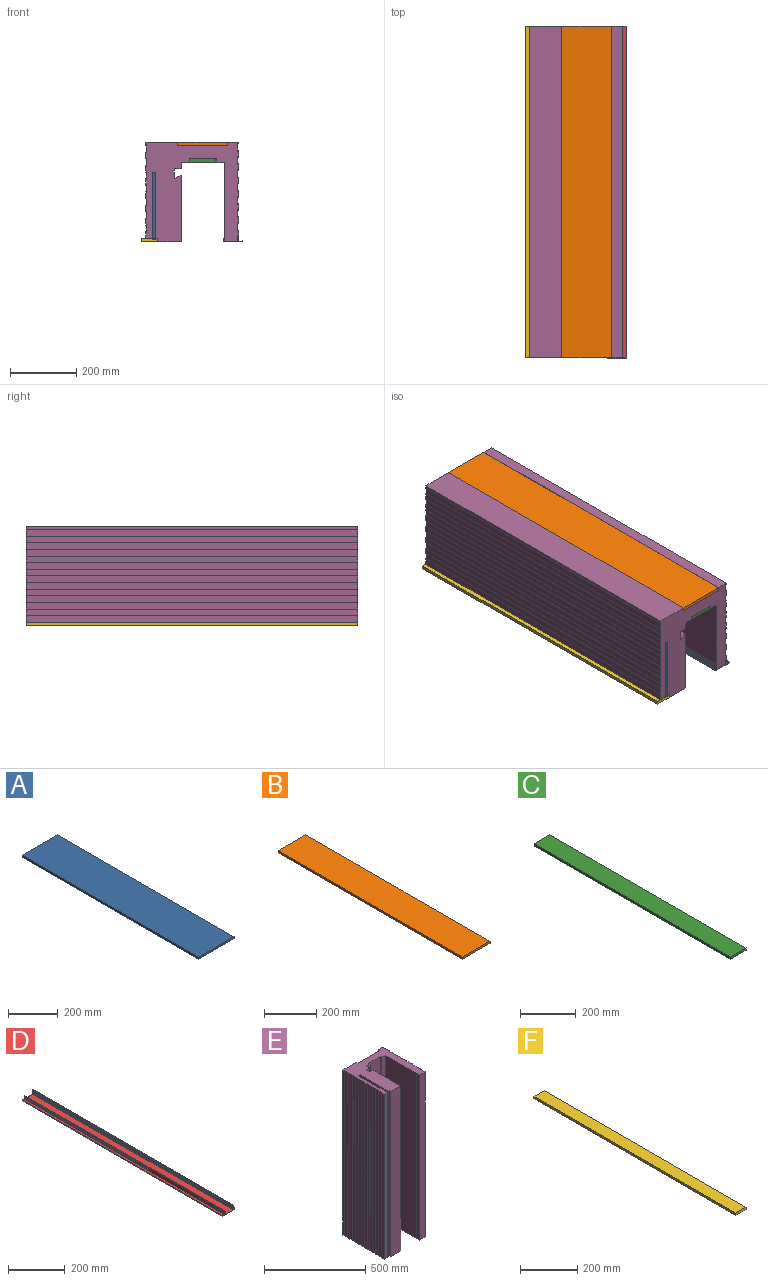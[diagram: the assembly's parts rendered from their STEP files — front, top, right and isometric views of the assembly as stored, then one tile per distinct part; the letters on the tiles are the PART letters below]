
ASSEMBLY  parts=6 mates=5
PART A: 6 faces, bbox 200x1000x10 mm
  f0: plane 1000x10mm, normal (-1,0,0), area 10000mm2, adj f1,f3,f4,f5
  f1: plane 1000x200mm, normal (0,0,-1), area 200000mm2, adj f0,f2,f4,f5
  f2: plane 1000x10mm, normal (1,0,0), area 10000mm2, adj f1,f3,f4,f5
  f3: plane 1000x200mm, normal (0,0,1), area 200000mm2, adj f0,f2,f4,f5
  f4: plane 200x10mm, normal (0,-1,0), area 2000mm2, adj f0,f1,f2,f3
  f5: plane 200x10mm, normal (0,1,0), area 2000mm2, adj f0,f1,f2,f3
PART B: 6 faces, bbox 150x1000x10 mm
  f0: plane 1000x10mm, normal (-1,0,0), area 10000mm2, adj f1,f3,f4,f5
  f1: plane 1000x150mm, normal (0,0,-1), area 150000mm2, adj f0,f2,f4,f5
  f2: plane 1000x10mm, normal (1,0,0), area 10000mm2, adj f1,f3,f4,f5
  f3: plane 1000x150mm, normal (0,0,1), area 150000mm2, adj f0,f2,f4,f5
  f4: plane 150x10mm, normal (0,-1,0), area 1500mm2, adj f0,f1,f2,f3
  f5: plane 150x10mm, normal (0,1,0), area 1500mm2, adj f0,f1,f2,f3
PART C: 6 faces, bbox 80x1000x10 mm
  f0: plane 1000x10mm, normal (-1,0,0), area 10000mm2, adj f1,f3,f4,f5
  f1: plane 1000x80mm, normal (0,0,-1), area 80000mm2, adj f0,f2,f4,f5
  f2: plane 1000x10mm, normal (1,0,0), area 10000mm2, adj f1,f3,f4,f5
  f3: plane 1000x80mm, normal (0,0,1), area 80000mm2, adj f0,f2,f4,f5
  f4: plane 80x10mm, normal (0,-1,0), area 800mm2, adj f0,f1,f2,f3
  f5: plane 80x10mm, normal (0,1,0), area 800mm2, adj f0,f1,f2,f3
PART D: 62 faces, bbox 57.5x1000x21 mm
  f0: plane 1000x14.3mm, normal (-1,0,0), area 14303.9mm2, adj f1,f2,f60,f61
  f1: plane 57.5x21mm, normal (0,-1,0), area 145.8mm2, adj f0,f2,f3,f4,f5,f6,f7,f8
  f2: plane 1000x11mm, normal (0,0,1), area 11000mm2, adj f0,f1,f3,f60
  f3: plane 1000x1.5mm, normal (1,0,0), area 1500mm2, adj f1,f2,f4,f60
  f4: plane 1000x1.5mm, normal (0,0,1), area 1500mm2, adj f1,f3,f5,f60
  f5: plane 1000x3mm, normal (-1,0,0), area 3000mm2, adj f1,f4,f6,f60
  f6: plane 1000x57.5mm, normal (0,0,-1), area 57500mm2, adj f1,f5,f7,f60
  f7: plane 1000x4mm, normal (1,0,0), area 4000mm2, adj f1,f6,f8,f60
  f8: plane 1000x1mm, normal (0,0,1), area 1000mm2, adj f1,f7,f9,f60
  f9: plane 1000x3mm, normal (-1,0,0), area 3000mm2, adj f1,f8,f10,f60
  f10: plane 1000x1mm, normal (0,0,1), area 1000mm2, adj f1,f9,f11,f60
  f11: plane 1000x7mm, normal (1,0,0), area 7000mm2, adj f1,f10,f12,f60
  f12: plane 1000x1mm, normal (0,0,-1), area 1000mm2, adj f1,f11,f13,f60
  f13: plane 1000x3mm, normal (-1,0,0), area 3000mm2, adj f1,f12,f14,f60
  f14: plane 1000x1mm, normal (0,0,-1), area 1000mm2, adj f1,f13,f15,f60
  f15: plane 1000x4mm, normal (1,0,0), area 4000mm2, adj f1,f14,f16,f60
  f16: plane 1000x2mm, normal (0,0,1), area 2000mm2, adj f1,f15,f17,f60
  f17: plane 1000x12mm, normal (1,0,0), area 12000mm2, adj f1,f16,f18,f60
  f18: plane 1000x1mm, normal (0,0,1), area 1000mm2, adj f1,f17,f19,f60
  f19: plane 1000x1.73mm, normal (-0.87,0,0.5), area 2000mm2, adj f1,f18,f20,f60
  f20: plane 1000x1mm, normal (0,0,-1), area 1000mm2, adj f1,f19,f21,f60
  f21: plane 1000x1.73mm, normal (-0.87,0,0.5), area 2000mm2, adj f1,f20,f22,f60
  f22: plane 1000x1mm, normal (0,0,-1), area 1000mm2, adj f1,f21,f23,f60
  f23: plane 1000x1.73mm, normal (-0.87,0,0.5), area 2000mm2, adj f1,f22,f24,f60
  f24: plane 1000x1mm, normal (0,0,-1), area 1000mm2, adj f1,f23,f25,f60
  f25: plane 1000x1.73mm, normal (-0.87,0,0.5), area 2000mm2, adj f1,f24,f26,f60
  f26: plane 1000x1mm, normal (0,0,-1), area 1000mm2, adj f1,f25,f27,f60
  f27: plane 1000x1.73mm, normal (-0.87,0,0.5), area 2000mm2, adj f1,f26,f28,f60
  f28: plane 1000x1mm, normal (0,0,-1), area 1000mm2, adj f1,f27,f29,f60
  f29: plane 1000x1.73mm, normal (-0.87,0,0.5), area 2000mm2, adj f1,f28,f30,f60
  f30: plane 1000x1mm, normal (0,0,-1), area 1000mm2, adj f1,f29,f31,f60
  f31: plane 1000x1.73mm, normal (-0.87,0,0.5), area 2000mm2, adj f1,f30,f32,f60
  f32: plane 1000x1mm, normal (0,0,-1), area 1000mm2, adj f1,f31,f33,f60
  f33: plane 1000x1.73mm, normal (-0.87,0,0.5), area 2000mm2, adj f1,f32,f34,f60
  f34: plane 1000x1mm, normal (0,0,-1), area 1000mm2, adj f1,f33,f35,f60
  f35: plane 1000x1.73mm, normal (-0.87,0,0.5), area 2000mm2, adj f1,f34,f36,f60
  f36: plane 1000x1mm, normal (0,0,-1), area 1000mm2, adj f1,f35,f37,f60
  f37: plane 1000x1.73mm, normal (-0.87,0,0.5), area 2000mm2, adj f1,f36,f38,f60
  f38: plane 1000x1mm, normal (0,0,-1), area 1000mm2, adj f1,f37,f39,f60
  f39: plane 1000x1.73mm, normal (-0.87,0,0.5), area 2000mm2, adj f1,f38,f40,f60
  f40: plane 1000x1mm, normal (0,0,-1), area 1000mm2, adj f1,f39,f41,f60
  f41: plane 1000x0.45mm, normal (-1,0,0), area 447.4mm2, adj f1,f40,f42,f60
  f42: plane 1000x41mm, normal (0,0,1), area 41000mm2, adj f1,f41,f43,f60
  f43: plane 1000x0.45mm, normal (1,0,0), area 447.4mm2, adj f1,f42,f44,f60
  f44: plane 1000x1mm, normal (0,0,-1), area 1000mm2, adj f1,f43,f45,f60
  f45: plane 1000x1.73mm, normal (0.87,0,0.5), area 2000mm2, adj f1,f44,f46,f60
  f46: plane 1000x1mm, normal (0,0,-1), area 1000mm2, adj f1,f45,f47,f60
  f47: plane 1000x1.73mm, normal (0.87,0,0.5), area 2000mm2, adj f1,f46,f48,f60
  f48: plane 1000x1mm, normal (0,0,-1), area 1000mm2, adj f1,f47,f49,f60
  f49: plane 1000x1.73mm, normal (0.87,0,0.5), area 2000mm2, adj f1,f48,f50,f60
  f50: plane 1000x1mm, normal (0,0,-1), area 1000mm2, adj f1,f49,f51,f60
  f51: plane 1000x1.73mm, normal (0.87,0,0.5), area 2000mm2, adj f1,f50,f52,f60
  f52: plane 1000x1mm, normal (0,0,-1), area 1000mm2, adj f1,f51,f53,f60
  f53: plane 1000x1.73mm, normal (0.87,0,0.5), area 2000mm2, adj f1,f52,f54,f60
  f54: plane 1000x1mm, normal (0,0,-1), area 1000mm2, adj f1,f53,f55,f60
  f55: plane 1000x1.73mm, normal (0.87,0,0.5), area 2000mm2, adj f1,f54,f56,f60
  f56: plane 1000x1mm, normal (0,0,-1), area 1000mm2, adj f1,f55,f57,f60
  f57: plane 1000x1.73mm, normal (0.87,0,0.5), area 2000mm2, adj f1,f56,f58,f60
  f58: plane 1000x1mm, normal (0,0,-1), area 1000mm2, adj f1,f57,f59,f60
  f59: plane 1000x1.73mm, normal (0.87,0,0.5), area 2000mm2, adj f1,f58,f60,f61
  f60: plane 57.5x21mm, normal (0,1,0), area 145.8mm2, adj f0,f2,f3,f4,f5,f6,f7,f8
  f61: plane 1000x1mm, normal (0,0,1), area 1000mm2, adj f0,f1,f59,f60
PART E: 88 faces, bbox 280x300x1000 mm
  f0: plane 1000x20mm, normal (-1,0,0), area 20000mm2, adj f44,f45,f82,f86
  f1: plane 1000x20mm, normal (-1,0,0), area 20000mm2, adj f44,f45,f79,f83
  f2: plane 1000x20mm, normal (-1,0,0), area 20000mm2, adj f44,f45,f76,f80
  f3: plane 1000x20mm, normal (-1,0,0), area 20000mm2, adj f44,f45,f73,f77
  f4: plane 1000x20mm, normal (-1,0,0), area 20000mm2, adj f44,f45,f70,f74
  f5: plane 1000x20mm, normal (-1,0,0), area 20000mm2, adj f44,f45,f67,f71
  f6: plane 1000x10mm, normal (-1,0,0), area 10000mm2, adj f15,f44,f45,f68
  f7: plane 1000x15mm, normal (1,0,0), area 15000mm2, adj f39,f44,f45,f64
  f8: plane 1000x20mm, normal (1,0,0), area 20000mm2, adj f44,f45,f61,f65
  f9: plane 1000x20mm, normal (1,0,0), area 20000mm2, adj f44,f45,f58,f62
  f10: plane 1000x20mm, normal (1,0,0), area 20000mm2, adj f44,f45,f55,f59
  f11: plane 1000x20mm, normal (1,0,0), area 20000mm2, adj f44,f45,f52,f56
  f12: plane 1000x20mm, normal (1,0,0), area 20000mm2, adj f44,f45,f49,f53
  f13: plane 1000x20mm, normal (1,0,0), area 20000mm2, adj f44,f45,f46,f50
  f14: plane 1000x10mm, normal (1,0,0), area 10000mm2, adj f15,f43,f44,f45
  f15: plane 1000x96.75mm, normal (0,1,0), area 96750mm2, adj f6,f14,f44,f45
  f16: plane 1000x20mm, normal (-1,0,0), area 20000mm2, adj f17,f44,f45,f85
  f17: plane 1000x20.5mm, normal (0,-1,0), area 20500mm2, adj f16,f18,f44,f45
  f18: plane 1000x200mm, normal (1,0,0), area 200000mm2, adj f17,f19,f44,f45
  f19: cylinder r=10mm len=1000mm, axis (0,0,-1), area 11054.3mm2, adj f18,f20,f44,f45
  f20: plane 1000x200mm, normal (-1,0,0), area 200000mm2, adj f19,f21,f44,f45
  f21: plane 1000x6mm, normal (0,-1,0), area 6000mm2, adj f20,f22,f44,f45
  f22: plane 1000x10mm, normal (-1,0,0), area 10000mm2, adj f21,f23,f44,f45
  f23: plane 1000x70mm, normal (0,-1,0), area 70000mm2, adj f22,f24,f44,f45
  f24: plane 1000x200.19mm, normal (1,0,0), area 200190.5mm2, adj f23,f25,f44,f45
  f25: plane 1000x20mm, normal (-0.45,0.89,0), area 22446.5mm2, adj f24,f26,f44,f45
  f26: plane 1000x30mm, normal (1,0,0), area 30000mm2, adj f25,f27,f44,f45
  f27: plane 1000x20mm, normal (0,-1,0), area 20000mm2, adj f26,f28,f44,f45
  f28: plane 1000x20mm, normal (1,0,0), area 20000mm2, adj f27,f29,f44,f45
  f29: plane 1000x24.75mm, normal (0,-1,0), area 24750mm2, adj f28,f30,f44,f45
  f30: plane 1000x10mm, normal (1,0,0), area 10000mm2, adj f29,f31,f44,f45
  f31: plane 1000x80.5mm, normal (0,-1,0), area 80500mm2, adj f30,f32,f44,f45
  f32: plane 1000x10mm, normal (-1,0,0), area 10000mm2, adj f31,f33,f44,f45
  f33: plane 1000x24.75mm, normal (0,-1,0), area 24750mm2, adj f32,f34,f44,f45
  f34: plane 1000x217.5mm, normal (-1,0,0), area 217500mm2, adj f33,f35,f44,f45
  f35: plane 1000x2mm, normal (0,-1,0), area 2000mm2, adj f34,f36,f44,f45
  f36: plane 1000x21.5mm, normal (-1,0,0), area 21500mm2, adj f35,f37,f44,f45
  f37: plane 1000x39.1mm, normal (0,-1,0), area 39100mm2, adj f36,f38,f44,f45
  f38: plane 1000x18.5mm, normal (1,0,0), area 18500mm2, adj f37,f39,f44,f45
  f39: plane 1000x1.9mm, normal (0,-1,0), area 1900mm2, adj f7,f38,f44,f45
  f40: plane 1000x5.5mm, normal (1,0,0), area 5500mm2, adj f41,f44,f45,f47
  f41: plane 1000x32.75mm, normal (0,1,0), area 32750mm2, adj f40,f42,f44,f45
  f42: plane 1000x10mm, normal (-1,0,0), area 10000mm2, adj f41,f43,f44,f45
  f43: plane 1000x150.5mm, normal (0,1,0), area 150500mm2, adj f14,f42,f44,f45
  f44: plane 300x280mm, normal (0,0,1), area 46795.3mm2, adj f0,f1,f2,f3,f4,f5,f6,f7
  f45: plane 300x280mm, normal (0,0,-1), area 46795.3mm2, adj f0,f1,f2,f3,f4,f5,f6,f7
  f46: plane 1000x2mm, normal (-0.71,0.71,0), area 2828.4mm2, adj f13,f44,f45,f48
  f47: plane 1000x2mm, normal (-0.71,-0.71,0), area 2828.4mm2, adj f40,f44,f45,f48
  f48: plane 1000x24mm, normal (1,0,0), area 24000mm2, adj f44,f45,f46,f47
  f49: plane 1000x2mm, normal (-0.71,0.71,0), area 2828.4mm2, adj f12,f44,f45,f51
  f50: plane 1000x2mm, normal (-0.71,-0.71,0), area 2828.4mm2, adj f13,f44,f45,f51
  f51: plane 1000x24mm, normal (1,0,0), area 24000mm2, adj f44,f45,f49,f50
  f52: plane 1000x2mm, normal (-0.71,0.71,0), area 2828.4mm2, adj f11,f44,f45,f54
  f53: plane 1000x2mm, normal (-0.71,-0.71,0), area 2828.4mm2, adj f12,f44,f45,f54
  f54: plane 1000x24mm, normal (1,0,0), area 24000mm2, adj f44,f45,f52,f53
  f55: plane 1000x2mm, normal (-0.71,0.71,0), area 2828.4mm2, adj f10,f44,f45,f57
  f56: plane 1000x2mm, normal (-0.71,-0.71,0), area 2828.4mm2, adj f11,f44,f45,f57
  f57: plane 1000x24mm, normal (1,0,0), area 24000mm2, adj f44,f45,f55,f56
  f58: plane 1000x2mm, normal (-0.71,0.71,0), area 2828.4mm2, adj f9,f44,f45,f60
  f59: plane 1000x2mm, normal (-0.71,-0.71,0), area 2828.4mm2, adj f10,f44,f45,f60
  f60: plane 1000x24mm, normal (1,0,0), area 24000mm2, adj f44,f45,f58,f59
  f61: plane 1000x2mm, normal (-0.71,0.71,0), area 2828.4mm2, adj f8,f44,f45,f63
  f62: plane 1000x2mm, normal (-0.71,-0.71,0), area 2828.4mm2, adj f9,f44,f45,f63
  f63: plane 1000x24mm, normal (1,0,0), area 24000mm2, adj f44,f45,f61,f62
  f64: plane 1000x2mm, normal (-0.71,0.71,0), area 2828.4mm2, adj f7,f44,f45,f66
  f65: plane 1000x2mm, normal (-0.71,-0.71,0), area 2828.4mm2, adj f8,f44,f45,f66
  f66: plane 1000x24mm, normal (1,0,0), area 24000mm2, adj f44,f45,f64,f65
  f67: plane 1000x2mm, normal (0.71,0.71,0), area 2828.4mm2, adj f5,f44,f45,f69
  f68: plane 1000x2mm, normal (0.71,-0.71,0), area 2828.4mm2, adj f6,f44,f45,f69
  f69: plane 1000x24mm, normal (-1,0,0), area 24000mm2, adj f44,f45,f67,f68
  f70: plane 1000x2mm, normal (0.71,0.71,0), area 2828.4mm2, adj f4,f44,f45,f72
  f71: plane 1000x2mm, normal (0.71,-0.71,0), area 2828.4mm2, adj f5,f44,f45,f72
  f72: plane 1000x24mm, normal (-1,0,0), area 24000mm2, adj f44,f45,f70,f71
  f73: plane 1000x2mm, normal (0.71,0.71,0), area 2828.4mm2, adj f3,f44,f45,f75
  f74: plane 1000x2mm, normal (0.71,-0.71,0), area 2828.4mm2, adj f4,f44,f45,f75
  f75: plane 1000x24mm, normal (-1,0,0), area 24000mm2, adj f44,f45,f73,f74
  f76: plane 1000x2mm, normal (0.71,0.71,0), area 2828.4mm2, adj f2,f44,f45,f78
  f77: plane 1000x2mm, normal (0.71,-0.71,0), area 2828.4mm2, adj f3,f44,f45,f78
  f78: plane 1000x24mm, normal (-1,0,0), area 24000mm2, adj f44,f45,f76,f77
  f79: plane 1000x2mm, normal (0.71,0.71,0), area 2828.4mm2, adj f1,f44,f45,f81
  f80: plane 1000x2mm, normal (0.71,-0.71,0), area 2828.4mm2, adj f2,f44,f45,f81
  f81: plane 1000x24mm, normal (-1,0,0), area 24000mm2, adj f44,f45,f79,f80
  f82: plane 1000x2mm, normal (0.71,0.71,0), area 2828.4mm2, adj f0,f44,f45,f84
  f83: plane 1000x2mm, normal (0.71,-0.71,0), area 2828.4mm2, adj f1,f44,f45,f84
  f84: plane 1000x24mm, normal (-1,0,0), area 24000mm2, adj f44,f45,f82,f83
  f85: plane 1000x2mm, normal (0.71,0.71,0), area 2828.4mm2, adj f16,f44,f45,f87
  f86: plane 1000x2mm, normal (0.71,-0.71,0), area 2828.4mm2, adj f0,f44,f45,f87
  f87: plane 1000x24mm, normal (-1,0,0), area 24000mm2, adj f44,f45,f85,f86
PART F: 6 faces, bbox 50x1000x10 mm
  f0: plane 1000x10mm, normal (-1,0,0), area 10000mm2, adj f1,f3,f4,f5
  f1: plane 1000x50mm, normal (0,0,-1), area 50000mm2, adj f0,f2,f4,f5
  f2: plane 1000x10mm, normal (1,0,0), area 10000mm2, adj f1,f3,f4,f5
  f3: plane 1000x50mm, normal (0,0,1), area 50000mm2, adj f0,f2,f4,f5
  f4: plane 50x10mm, normal (0,-1,0), area 500mm2, adj f0,f1,f2,f3
  f5: plane 50x10mm, normal (0,1,0), area 500mm2, adj f0,f1,f2,f3
PLACE A rot(axis=(0,1,0),90deg) t=(-266.83,500,-26.72)mm
PLACE B t=(-190.83,500,55.28)mm fixed
PLACE C t=(-155.83,500,5.28)mm
PLACE D rot(axis=(0,0,1),180deg) t=(-52.58,-500,-235.22)mm
PLACE E rot(axis=(1,0,0),90deg) t=(-169.34,500,-104.89)mm
PLACE F t=(-300.58,500,-234.72)mm
MATE fastened A.f4 <-> E.f44  axis (0,-1,0) through (-256.58,-500,-24.72)mm
MATE fastened E.f44 <-> B.f4  axis (0,-1,0) through (-190.83,-500,65.28)mm
MATE fastened C.f4 <-> E.f44  axis (0,-1,0) through (-155.83,-500,15.28)mm
MATE fastened D.f60 <-> E.f44  axis (0,-1,0) through (-48.58,-500,-233.72)mm
MATE fastened F.f4 <-> E.f44  axis (0,-1,0) through (-250.58,-500,-224.72)mm
